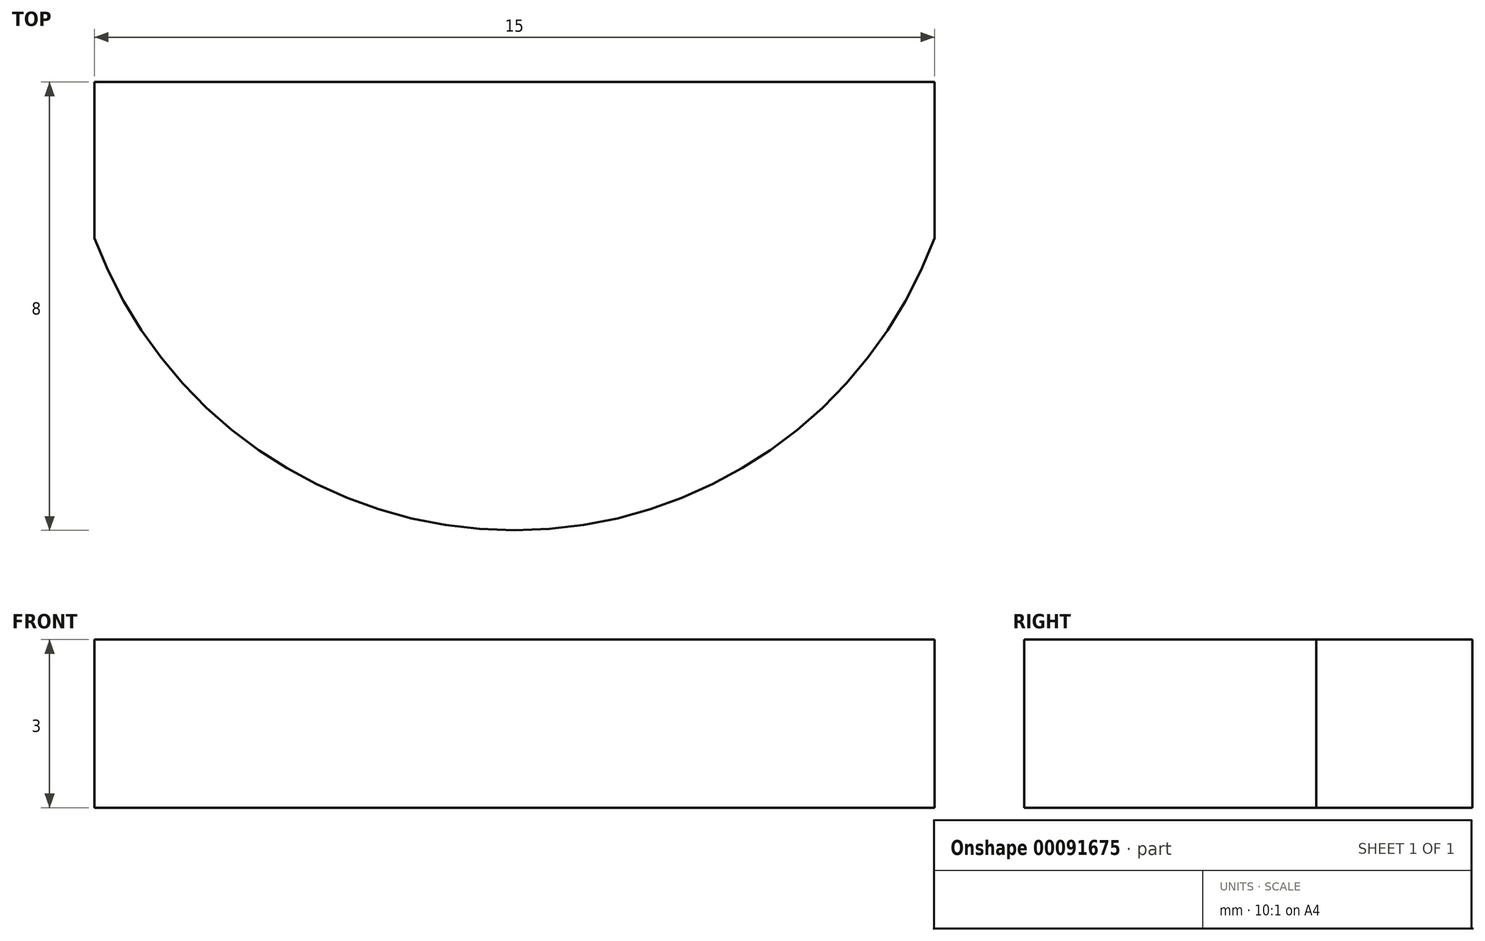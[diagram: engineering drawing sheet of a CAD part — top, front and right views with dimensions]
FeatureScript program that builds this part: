
annotation { "Feature Type Name" : "Feature", "Feature Type Description" : "" }
export const myFeature = defineFeature(function(context is Context, id is Id, definition is map)
    precondition{}
    {
        {
            var Q0;
            Q0=qCreatedBy(makeId("Top.planeOp"),FACE);
            var sketch = newSketch(context, id + "F0", { "sketchPlane" : qUnion([Q0])});
            skArc(sketch, "E0", {"start": v(-7.5, -2.78) * mm, "mid": v(0, -8) * mm, "end": v(7.5, -2.78) * mm});
            skLineSegment(sketch, "E1", {"start": v(-7.5, 0) * mm, "end": v(7.5, 0) * mm});
            skLineSegment(sketch, "E2", {"start": v(-7.5, 0) * mm, "end": v(-7.5, -2.78) * mm});
            skLineSegment(sketch, "E3.MirrorCS", {"start": v(7.5, 0) * mm, "end": v(7.5, -2.78) * mm});
            skSolve(sketch);
        }
        {
            var Q0;
            Q0 = qSketchRegion(id + "F0", true);
            extrude(context, id + "F1", {"entities" : qUnion([Q0]), "depth" : 3 * mm});
        }
    });
